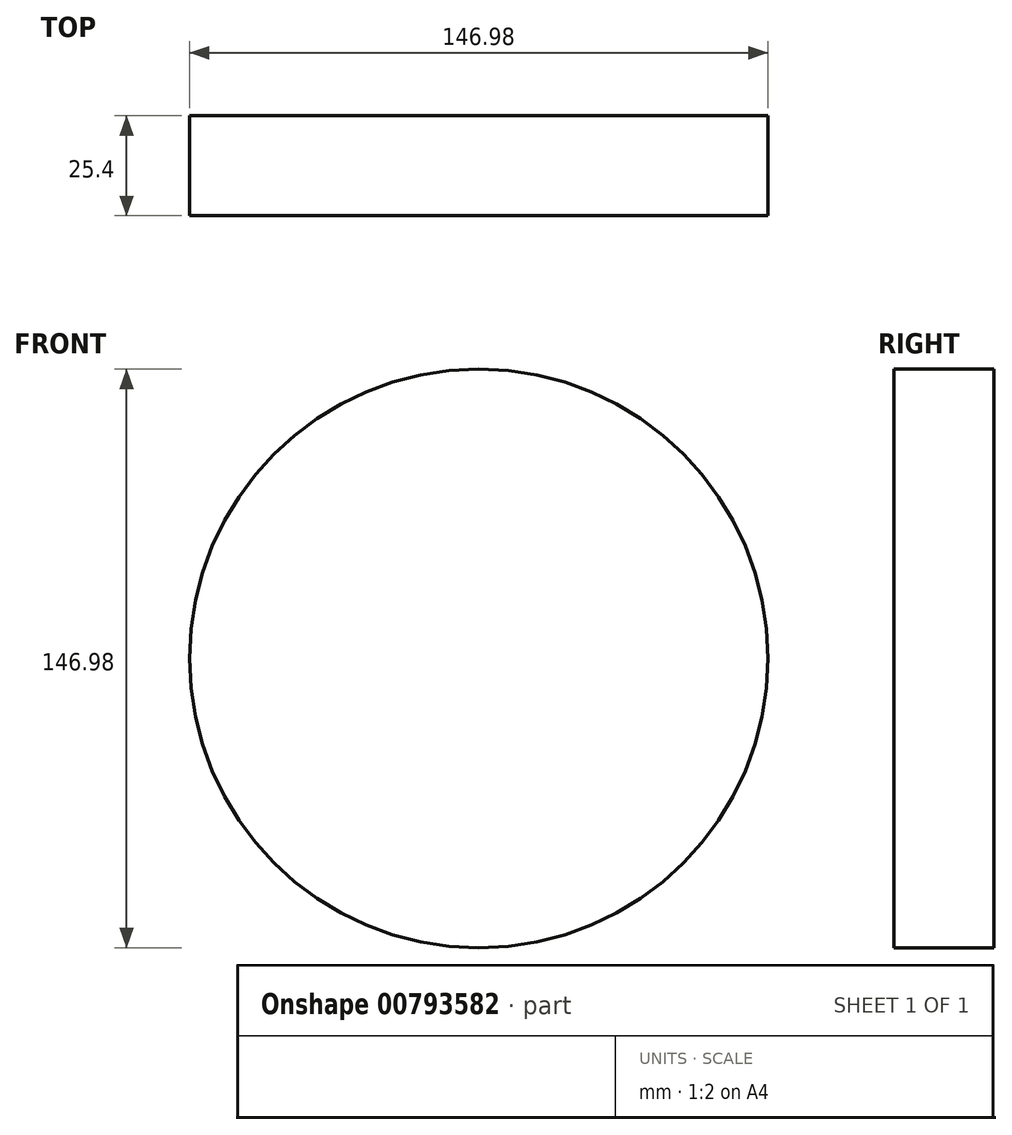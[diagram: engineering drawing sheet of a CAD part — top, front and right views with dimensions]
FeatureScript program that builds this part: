
annotation { "Feature Type Name" : "Feature", "Feature Type Description" : "" }
export const myFeature = defineFeature(function(context is Context, id is Id, definition is map)
    precondition{}
    {
        {
            var Q0;
            Q0=qCreatedBy(makeId("Front.planeOp"),FACE);
            var sketch = newSketch(context, id + "F0", { "sketchPlane" : qUnion([Q0])});
            skCircle(sketch, "E0", {"center": v(0, 0) * mm, "radius": 73.5 * mm});
            skSolve(sketch);
        }
        {
            var Q0;
            Q0 = qSketchRegion(id + "F0", true);
            extrude(context, id + "F1", {"entities" : qUnion([Q0]), "depth" : 25.4 * mm, "offsetDistance" : 25.4 * mm});
        }
    });
